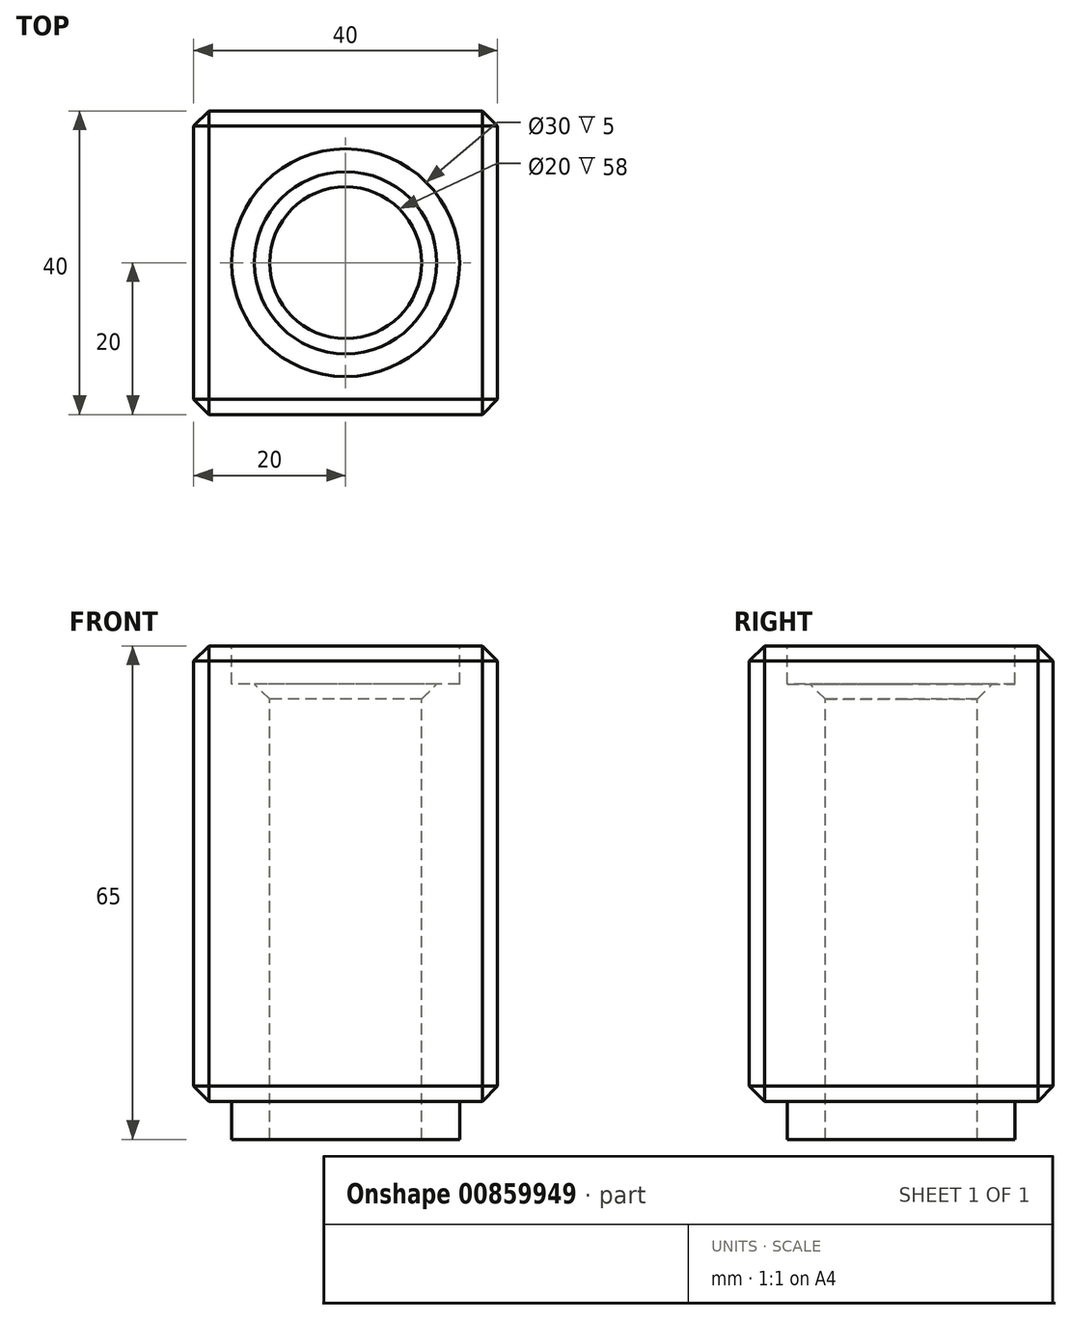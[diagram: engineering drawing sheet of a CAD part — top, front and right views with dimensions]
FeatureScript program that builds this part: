
annotation { "Feature Type Name" : "Feature", "Feature Type Description" : "" }
export const myFeature = defineFeature(function(context is Context, id is Id, definition is map)
    precondition{}
    {
        {
            var Q0;
            Q0=qCreatedBy(makeId("Top.planeOp"),FACE);
            var sketch = newSketch(context, id + "F0", { "sketchPlane" : qUnion([Q0])});
            skLineSegment(sketch, "E0.bottom", {"start": v(-20, 20) * mm, "end": v(20, 20) * mm});
            skLineSegment(sketch, "E0.top", {"start": v(-20, -20) * mm, "end": v(20, -20) * mm});
            skLineSegment(sketch, "E0.left", {"start": v(-20, 20) * mm, "end": v(-20, -20) * mm});
            skLineSegment(sketch, "E0.right", {"start": v(20, 20) * mm, "end": v(20, -20) * mm});
            skSolve(sketch);
        }
        {
            var Q0;
            Q0=makeQuery(id+"F0.imprint","IMPRINT",FACE,{"disambiguationData":[TD([[makeQuery(id+"F0.imprint","IMPRINT",EDGE,{"derivedFrom":sQuery(id+"F0.wireOp",EDGE,"E0.bottom")}),-1.0]])]});
            extrude(context, id + "F1", {"entities" : qUnion([Q0]), "depth" : 60 * mm, "offsetDistance" : 25 * mm});
        }
        {
            var Q0;
            Q0=makeQuery(id+"F1.opExtrude","CAP_FACE",FACE,{"disambiguationData":[OSD([sQuery(id+"F0.wireOp",EDGE,"E0.bottom"),sQuery(id+"F0.wireOp",EDGE,"E0.top"),sQuery(id+"F0.wireOp",EDGE,"E0.left"),sQuery(id+"F0.wireOp",EDGE,"E0.right")])],"isStart":false});
            var sketch = newSketch(context, id + "F2", { "sketchPlane" : qUnion([Q0])});
            skCircle(sketch, "E1", {"center": v(0, 0) * mm, "radius": 15 * mm});
            skSolve(sketch);
        }
        {
            var Q0;
            Q0 = qSketchRegion(id + "F2", true);
            var Q1;
            Q1=makeQuery(id+"F1.opExtrude","CAP_FACE",FACE,{"disambiguationData":[OSD([sQuery(id+"F0.wireOp",EDGE,"E0.bottom"),sQuery(id+"F0.wireOp",EDGE,"E0.top"),sQuery(id+"F0.wireOp",EDGE,"E0.left"),sQuery(id+"F0.wireOp",EDGE,"E0.right")])],"isStart":true});
            extrude(context, id + "F3", {"entities" : qUnion([Q0]), "operationType" : NewBodyOperationType.REMOVE, "endBound" : BoundingType.UP_TO_SURFACE, "oppositeDirection" : true, "depth" : 25 * mm, "endBoundEntityFace" : qUnion([Q1]), "offsetDistance" : 25 * mm});
        }
        {
            var Q0;
            Q0=makeQuery(id+"F1.opExtrude","CAP_FACE",FACE,{"disambiguationData":[OSD([sQuery(id+"F0.wireOp",EDGE,"E0.bottom"),sQuery(id+"F0.wireOp",EDGE,"E0.top"),sQuery(id+"F0.wireOp",EDGE,"E0.left"),sQuery(id+"F0.wireOp",EDGE,"E0.right")])],"isStart":false});
            var sketch = newSketch(context, id + "F4", { "sketchPlane" : qUnion([Q0])});
            skCircle(sketch, "E2", {"center": v(0, 0) * mm, "radius": 15 * mm});
            skCircle(sketch, "E3", {"center": v(0, 0) * mm, "radius": 10 * mm});
            skSolve(sketch);
        }
        {
            var Q0;
            Q0=makeQuery(id+"F4.imprint","IMPRINT",FACE,{"disambiguationData":[TD([[makeQuery(id+"F4.imprint","IMPRINT",EDGE,{"derivedFrom":sQuery(id+"F4.wireOp",EDGE,"E2")}),1.0]])]});
            extrude(context, id + "F5", {"entities" : qUnion([Q0]), "operationType" : NewBodyOperationType.ADD, "oppositeDirection" : true, "depth" : 65 * mm, "offsetDistance" : 25 * mm, "hasSecondDirection" : true, "secondDirectionOppositeDirection" : true, "secondDirectionDepth" : 5 * mm});
        }
        {
            var Q0;
            Q0=makeQuery(id+"F1.opExtrude","SWEPT_EDGE",EDGE,{"disambiguationData":[OSD([sQuery(id+"F0.wireOp",EDGE,"E0.top"),sQuery(id+"F0.wireOp",EDGE,"E0.left")])]});
            var Q1;
            Q1=makeQuery(id+"F1.opExtrude","SWEPT_EDGE",EDGE,{"disambiguationData":[OSD([sQuery(id+"F0.wireOp",EDGE,"E0.top"),sQuery(id+"F0.wireOp",EDGE,"E0.right")])]});
            var Q2;
            Q2=makeQuery(id+"F1.opExtrude","CAP_EDGE",EDGE,{"disambiguationData":[OSD([sQuery(id+"F0.wireOp",EDGE,"E0.top")])],"isStart":false});
            var Q3;
            Q3=makeQuery(id+"F1.opExtrude","CAP_EDGE",EDGE,{"disambiguationData":[OSD([sQuery(id+"F0.wireOp",EDGE,"E0.top")])],"isStart":true});
            var Q4;
            Q4=makeQuery(id+"F1.opExtrude","CAP_EDGE",EDGE,{"disambiguationData":[OSD([sQuery(id+"F0.wireOp",EDGE,"E0.right")])],"isStart":true});
            var Q5;
            Q5=makeQuery(id+"F1.opExtrude","SWEPT_EDGE",EDGE,{"disambiguationData":[OSD([sQuery(id+"F0.wireOp",EDGE,"E0.bottom"),sQuery(id+"F0.wireOp",EDGE,"E0.right")])]});
            var Q6;
            Q6=makeQuery(id+"F1.opExtrude","CAP_EDGE",EDGE,{"disambiguationData":[OSD([sQuery(id+"F0.wireOp",EDGE,"E0.right")])],"isStart":false});
            var Q7;
            Q7=makeQuery(id+"F1.opExtrude","CAP_EDGE",EDGE,{"disambiguationData":[OSD([sQuery(id+"F0.wireOp",EDGE,"E0.left")])],"isStart":false});
            var Q8;
            Q8=makeQuery(id+"F1.opExtrude","CAP_EDGE",EDGE,{"disambiguationData":[OSD([sQuery(id+"F0.wireOp",EDGE,"E0.bottom")])],"isStart":false});
            var Q9;
            Q9=makeQuery(id+"F1.opExtrude","SWEPT_EDGE",EDGE,{"disambiguationData":[OSD([sQuery(id+"F0.wireOp",EDGE,"E0.bottom"),sQuery(id+"F0.wireOp",EDGE,"E0.left")])]});
            var Q10;
            Q10=makeQuery(id+"F1.opExtrude","CAP_EDGE",EDGE,{"disambiguationData":[OSD([sQuery(id+"F0.wireOp",EDGE,"E0.left")])],"isStart":true});
            var Q11;
            Q11=makeQuery(id+"F1.opExtrude","CAP_EDGE",EDGE,{"disambiguationData":[OSD([sQuery(id+"F0.wireOp",EDGE,"E0.bottom")])],"isStart":true});
            var Q12;
            Q12=makeQuery(id+"F3.boolean.opBoolean","COPY",EDGE,{"derivedFrom":makeQuery(id+"F3.opExtrude","CAP_EDGE",EDGE,{"disambiguationData":[OSD([sQuery(id+"F2.wireOp",EDGE,"E1")])],"isStart":true})});
            var Q13;
            Q13=makeQuery(id+"F5.opExtrude","CAP_EDGE",EDGE,{"disambiguationData":[OSD([sQuery(id+"F4.wireOp",EDGE,"E3")])],"isStart":true});
            chamfer(context, id + "F6", {"entities" : qUnion([Q0, Q1, Q2, Q3, Q4, Q5, Q6, Q7, Q8, Q9, Q10, Q11, Q12, Q13]), "width" : 2 * mm, "tangentPropagation" : true});
        }
    });
